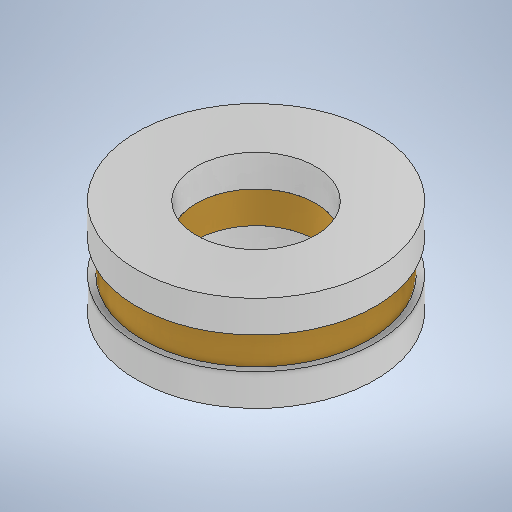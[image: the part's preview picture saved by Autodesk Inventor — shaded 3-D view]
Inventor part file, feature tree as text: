
AUTODESK INVENTOR PART (.ipt)
format: ipt  version: 2025.2 (Build 292293000, 293)  size: 264,192 bytes
history: native  units: mm
features: extrude x4, sketch x4
ambient origin geometry x8: Origin, YZ Plane, XZ Plane, XY Plane, X Axis, Y Axis, Z Axis, Center Point
bodies: Solid1 (feature_tree), Solid2 (feature_tree), Solid3 (feature_tree)
feature tree (8):
  extrude  "Extrusion1"  Depth=1.333333mm TaperAngle=0.0deg
  extrude  "Extrusion2"  Depth=1.333333mm TaperAngle=0.0deg
  extrude  "Extrusion3"  Depth=5.0mm
  extrude  "Extrusion4"  Depth=10.0mm
  sketch  "Sketch1"  dims[d0=10.0mm d1=1.333333mm d2=0.0mm]
  sketch  "Sketch2"  dims[d3=9.5mm d4=1.333333mm d5=0.0mm]
  sketch  "Sketch3"  dims[d6=1.333333mm d7=0.0mm d8=5.0mm]
  sketch  "Sketch4"  dims[d9=10.0mm d10=0.0mm d11=0.5mm d12=0.872665mm]
